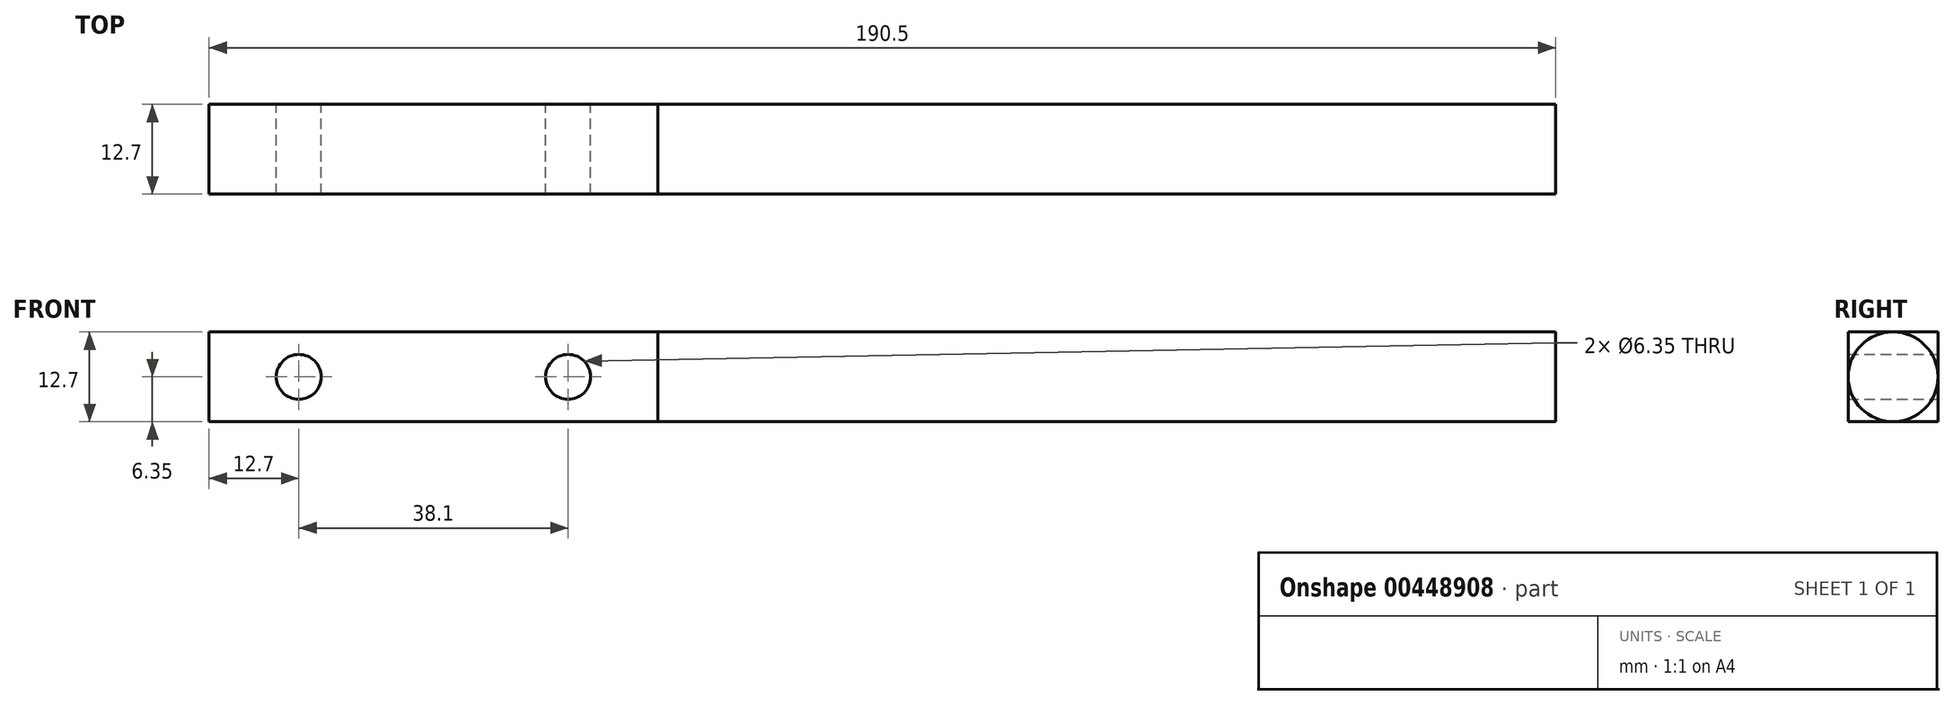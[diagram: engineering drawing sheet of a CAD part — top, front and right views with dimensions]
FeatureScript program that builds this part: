
annotation { "Feature Type Name" : "Feature", "Feature Type Description" : "" }
export const myFeature = defineFeature(function(context is Context, id is Id, definition is map)
    precondition{}
    {
        {
            var Q0;
            Q0=qCreatedBy(makeId("Front.planeOp"),FACE);
            var sketch = newSketch(context, id + "F0", { "sketchPlane" : qUnion([Q0])});
            skLineSegment(sketch, "E0.bottom", {"start": v(-50.8, 6.35) * mm, "end": v(12.7, 6.35) * mm});
            skLineSegment(sketch, "E0.top", {"start": v(-50.8, -6.35) * mm, "end": v(12.7, -6.35) * mm});
            skLineSegment(sketch, "E0.left", {"start": v(-50.8, 6.35) * mm, "end": v(-50.8, -6.35) * mm});
            skLineSegment(sketch, "E0.right", {"start": v(12.7, 6.35) * mm, "end": v(12.7, -6.35) * mm});
            skCircle(sketch, "E1", {"center": v(0, 0) * mm, "radius": 3.18 * mm});
            skCircle(sketch, "E2", {"center": v(-38.1, 0) * mm, "radius": 3.18 * mm});
            skSolve(sketch);
        }
        {
            var Q0;
            Q0 = qSketchRegion(id + "F0", true);
            extrude(context, id + "F1", {"entities" : qUnion([Q0]), "depth" : 12.7 * mm});
        }
        {
            var Q0;
            Q0=makeQuery(id+"F1.opExtrude","SWEPT_FACE",FACE,{"disambiguationData":[OSD([sQuery(id+"F0.wireOp",EDGE,"E0.right")])]});
            var sketch = newSketch(context, id + "F2", { "sketchPlane" : qUnion([Q0])});
            skCircle(sketch, "E3", {"center": v(-6.35, 0) * mm, "radius": 6.35 * mm});
            skSolve(sketch);
        }
        {
            var Q0;
            Q0 = qSketchRegion(id + "F2", true);
            extrude(context, id + "F3", {"entities" : qUnion([Q0]), "operationType" : NewBodyOperationType.ADD, "depth" : 127 * mm});
        }
    });
